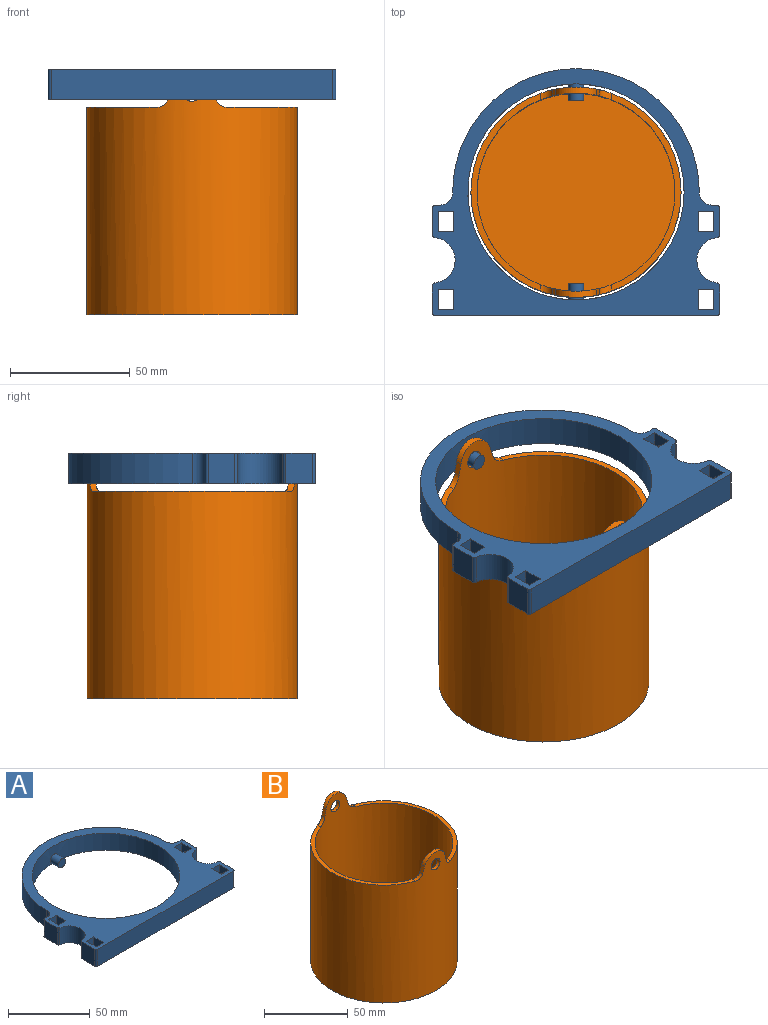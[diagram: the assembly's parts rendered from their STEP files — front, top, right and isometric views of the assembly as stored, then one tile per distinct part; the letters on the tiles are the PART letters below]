
ASSEMBLY  parts=2 mates=1
PART A: 45 faces, bbox 119.9x102.9x12.7 mm
  f0: cylinder r=45.09mm len=90.17mm, axis (0,0,-1), area 3534.1mm2, adj f27,f28,f30,f31
  f1: plane 12.7x8.38mm, normal (1,0,0), area 106.5mm2, adj f2,f26,f27,f28
  f2: plane 12.7x6.35mm, normal (0,-1,0), area 80.6mm2, adj f1,f3,f27,f28
  f3: plane 12.7x8.38mm, normal (-1,0,0), area 106.5mm2, adj f2,f26,f27,f28
  f4: plane 12.7x6.35mm, normal (0,1,0), area 80.6mm2, adj f5,f22,f27,f28
  f5: plane 12.7x8.38mm, normal (1,0,0), area 106.5mm2, adj f4,f6,f27,f28
  f6: plane 12.7x6.35mm, normal (0,-1,0), area 80.6mm2, adj f5,f22,f27,f28
  f7: plane 12.7x6.35mm, normal (0,1,0), area 80.6mm2, adj f8,f23,f27,f28
  f8: plane 12.7x8.38mm, normal (1,0,0), area 106.5mm2, adj f7,f9,f27,f28
  f9: plane 12.7x6.35mm, normal (0,-1,0), area 80.6mm2, adj f8,f23,f27,f28
  f10: plane 12.7x8.38mm, normal (-1,0,0), area 95.1mm2, adj f11,f24,f27,f28,f34
  f11: plane 12.7x6.35mm, normal (0,1,0), area 80.6mm2, adj f10,f12,f27,f28
  f12: plane 12.7x8.38mm, normal (1,0,0), area 106.5mm2, adj f11,f24,f27,f28
  f13: cylinder r=51.44mm len=102.87mm, axis (0,0,-1), area 2061mm2, adj f27,f28,f43,f44
  f14: plane 12.7x2.16mm, normal (0,1,0), area 27.4mm2, adj f27,f28,f39,f43
  f15: plane 12.7x11mm, normal (-1,0,0), area 139.7mm2, adj f27,f28,f39,f40
  f16: cylinder r=9.53mm len=18.92mm, axis (0,0,-1), area 351.5mm2, adj f27,f28,f40,f41
  f17: plane 12.7x11mm, normal (-1,0,0), area 139.7mm2, adj f27,f28,f41,f42
  f18: plane 117.35x12.7mm, normal (0,-1,0), area 1490.3mm2, adj f27,f28,f38,f42
  f19: plane 12.7x11mm, normal (1,0,0), area 128.3mm2, adj f27,f28,f33,f35,f38
  f20: cylinder r=9.53mm len=18.92mm, axis (0,0,-1), area 351.5mm2, adj f27,f28,f35,f36
  f21: plane 12.7x11mm, normal (1,0,0), area 128.3mm2, adj f27,f28,f34,f36,f37
  f22: plane 12.7x8.38mm, normal (-1,0,0), area 106.5mm2, adj f4,f6,f27,f28
  f23: plane 12.7x8.38mm, normal (-1,0,0), area 95.1mm2, adj f7,f9,f27,f28,f33
  f24: plane 12.7x6.35mm, normal (0,-1,0), area 80.6mm2, adj f10,f12,f27,f28
  f25: plane 12.7x2.16mm, normal (0,1,0), area 27.4mm2, adj f27,f28,f37,f44
  f26: plane 12.7x6.35mm, normal (0,1,0), area 80.6mm2, adj f1,f3,f27,f28
  f27: plane 119.89x102.87mm, normal (0,0,1), area 3354mm2, adj f0,f1,f2,f3,f4,f5,f6,f7
  f28: plane 119.89x102.87mm, normal (0,0,-1), area 3354mm2, adj f0,f1,f2,f3,f4,f5,f6,f7
  f29: plane 6.35x6.35mm, normal (0,1,0), area 31.7mm2, adj f30
  f30: cylinder r=3.17mm len=6.99mm, axis (0,1,0), area 138.2mm2, adj f0,f29
  f31: cylinder r=3.17mm len=6.99mm, axis (0,-1,0), area 138.2mm2, adj f0,f32
  f32: plane 6.35x6.35mm, normal (0,-1,0), area 31.7mm2, adj f31
  f33: cylinder r=1.91mm len=3.81mm, axis (1,0,0), area 30.4mm2, adj f19,f23
  f34: cylinder r=1.91mm len=3.81mm, axis (1,0,0), area 30.4mm2, adj f10,f21
  f35: cylinder r=1.27mm len=12.7mm, axis (0,0,-1), area 23.4mm2, adj f19,f20,f27,f28
  f36: cylinder r=1.27mm len=12.7mm, axis (0,0,-1), area 23.4mm2, adj f20,f21,f27,f28
  f37: cylinder r=1.27mm len=12.7mm, axis (0,0,1), area 25.3mm2, adj f21,f25,f27,f28
  f38: cylinder r=1.27mm len=12.7mm, axis (0,0,-1), area 25.3mm2, adj f18,f19,f27,f28
  f39: cylinder r=1.27mm len=12.7mm, axis (0,0,-1), area 25.3mm2, adj f14,f15,f27,f28
  f40: cylinder r=1.27mm len=12.7mm, axis (0,0,-1), area 23.4mm2, adj f15,f16,f27,f28
  f41: cylinder r=1.27mm len=12.7mm, axis (0,0,-1), area 23.4mm2, adj f16,f17,f27,f28
  f42: cylinder r=1.27mm len=12.7mm, axis (0,0,1), area 25.3mm2, adj f17,f18,f27,f28
  f43: cylinder r=5.08mm len=12.7mm, axis (0,0,-1), area 101.8mm2, adj f13,f14,f27,f28
  f44: cylinder r=5.08mm len=12.7mm, axis (0,0,-1), area 101.8mm2, adj f13,f25,f27,f28
PART B: 18 faces, bbox 87.6x87.6x101.6 mm
  f0: cylinder r=41.27mm len=99.06mm, axis (0,0,-1), area 22167.1mm2, adj f1,f2,f3,f4,f5,f6,f7,f8
  f1: plane 82.55x82.55mm, normal (0,0,1), area 5352.1mm2, adj f0
  f2: cylinder r=3.81mm len=7.62mm, axis (0,1,0), area 60.9mm2, adj f0,f13
  f3: cylinder r=3.81mm len=7.62mm, axis (0,1,0), area 60.9mm2, adj f0,f13
  f4: plane 82.48x29.01mm, normal (0,0,1), area 262.7mm2, adj f0,f13,f15,f17
  f5: plane 82.48x29.01mm, normal (0,0,1), area 262.7mm2, adj f0,f13,f14,f16
  f6: plane 4.89x2.9mm, normal (-0.97,0,0.26), area 13.2mm2, adj f0,f10,f13,f16
  f7: plane 4.89x2.9mm, normal (-0.97,0,0.26), area 13.2mm2, adj f0,f11,f13,f14
  f8: plane 4.89x2.9mm, normal (0.97,0,0.26), area 13.2mm2, adj f0,f11,f13,f15
  f9: plane 4.89x2.9mm, normal (0.97,0,0.26), area 13.2mm2, adj f0,f10,f13,f17
  f10: cylinder r=8.89mm len=17.17mm, axis (0,1,0), area 59.6mm2, adj f0,f6,f9,f13
  f11: cylinder r=8.89mm len=17.17mm, axis (0,1,0), area 59.6mm2, adj f0,f7,f8,f13
  f12: plane 87.63x87.63mm, normal (0,0,-1), area 6031.1mm2, adj f13
  f13: cylinder r=43.81mm len=101.6mm, axis (0,0,-1), area 24203.7mm2, adj f2,f3,f4,f5,f6,f7,f8,f9
  f14: cylinder r=5.08mm len=4.91mm, axis (0,-1,0), area 17.6mm2, adj f0,f5,f7,f13
  f15: cylinder r=5.08mm len=4.91mm, axis (0,-1,0), area 17.6mm2, adj f0,f4,f8,f13
  f16: cylinder r=5.08mm len=4.91mm, axis (0,-1,0), area 17.6mm2, adj f0,f5,f6,f13
  f17: cylinder r=5.08mm len=4.91mm, axis (0,-1,0), area 17.6mm2, adj f0,f4,f9,f13
PLACE A t=(0,0.07,6.35)mm
PLACE B t=(0,0,-89.54)mm
MATE slider B.f2 <-> A.f30  axis (0,1,0) through (0,41.08,3.17)mm
